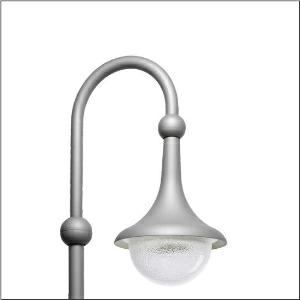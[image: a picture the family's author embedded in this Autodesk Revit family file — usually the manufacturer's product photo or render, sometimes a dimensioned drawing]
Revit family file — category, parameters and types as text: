
# Revit family: kleine_glocke___st1_2a_5xa1573k1b208_586f
name_source: partatom
category: Lighting Fixtures
units: mm (PartAtom-declared; Revit-internal decimal feet)

## family parameters
Cut with Voids When Loaded = No
Host = Face
Light Source = No
Part Type = Normal
Room Calculation Point = No
Round Connector Dimension = Use Diameter
Shared = No

## types (1)
- --- (1 x LED, 1750 lm, 13.2 W, 4000K)
    Apparent Load = 13 VA
    CIE Flux Codes = 28 64 93 98 100
    Color Rendering = 70
    Color Temperature = 4000K
    Default Elevation = 1800 mm
    Description = Small Bell, mast luminaire, primary light control with 3 zone facetted reflector, of plastic, aluminium vaporised, primary optical cover: enclosure, of PMMA, transparent structured, light distribution: ST1.2a, light emission: direct distribution, primary light characteristic: asymmetric, installation type: suspended mounting, LED, High Power LED, rated luminous flux: 1.750lm, luminous efficacy: 133lm/W, light colour: 740, colour temperature: 4000K, control gear: ECG Plus, control: flexible luminous flux parameterisation, time-dependent luminous flux control, constant luminous flux control, digital communication interface, power reduction, electronic power reduction, mains connection: 230..240V, AC, 50/60Hz, start of lifetime: 13W, end of service life: 14W, reduction: 7W, luminaire housing, bell-shaped, of glass-fibre reinforced polyester, coated, Siteco® metallic grey (DB 702S), please order curved mast extension separately, diameter: 430mm, height: 575mm, protection rating (complete): IP54, insulation class (complete): insulation class II (safety insulation), certification: CE, ENEC, VDE, impact resistance: IK07, standard-compliant lighting for roads and squares, packaging unit: 1 piece

Light Distribution: ST1.2a
    Height = 575 mm
    Lamp = 1 x LED
    Lamp Light Flux = 1750 lm
    Lamp Power = 13.2 W
    Lamp count = 1
    Length = 430 mm
    Luminous efficacy = 133 lm/W
    Manufacturer = Siteco
    ModVariant = No
    Model = 5XA1573K1B208
    Number of Poles = 1
    OnlyDefault = Yes
    Power Factor = 1
    Product Name = Kleine Glocke | ST1.2a
    Product group = mast luminaire | pylon annexe
    ProductGroupID = 6201
    Protection Class = Protection class II
    Protection Degree = IP 54
    RLX_Detail_Level = 1
    RLX_Emergency_Light_Flux = 0 lm
    RLX_Emergency_Type = 0
    RLX_Emergency_Type_DB = No
    RlxData = <blob elided: 51965 chars, md5=03db7a1c>
    Socket = socket
    Standby Power = 0 W
    System Light Flux = 1750 lm
    System Power = 13 W
    Type Comments = factory setting: luminous flux: 100 % | dim-lin: 254 | 249 mA
    Type Image = l_1284392.jpg
    URL = http://relux.com
    VarID = @adj_171975
    Voltage = 0 V
    Weight = 0.00 kg
    Width = 0 mm  [stored 0 ft]

note: [stored X ft] marks values corroborated as IEEE doubles in the binary element streams (Revit-internal decimal feet)

## geometry (parser evidence)
native form markers: Blend x4, Sweep x10
no freeform markers — native parametric forms only
